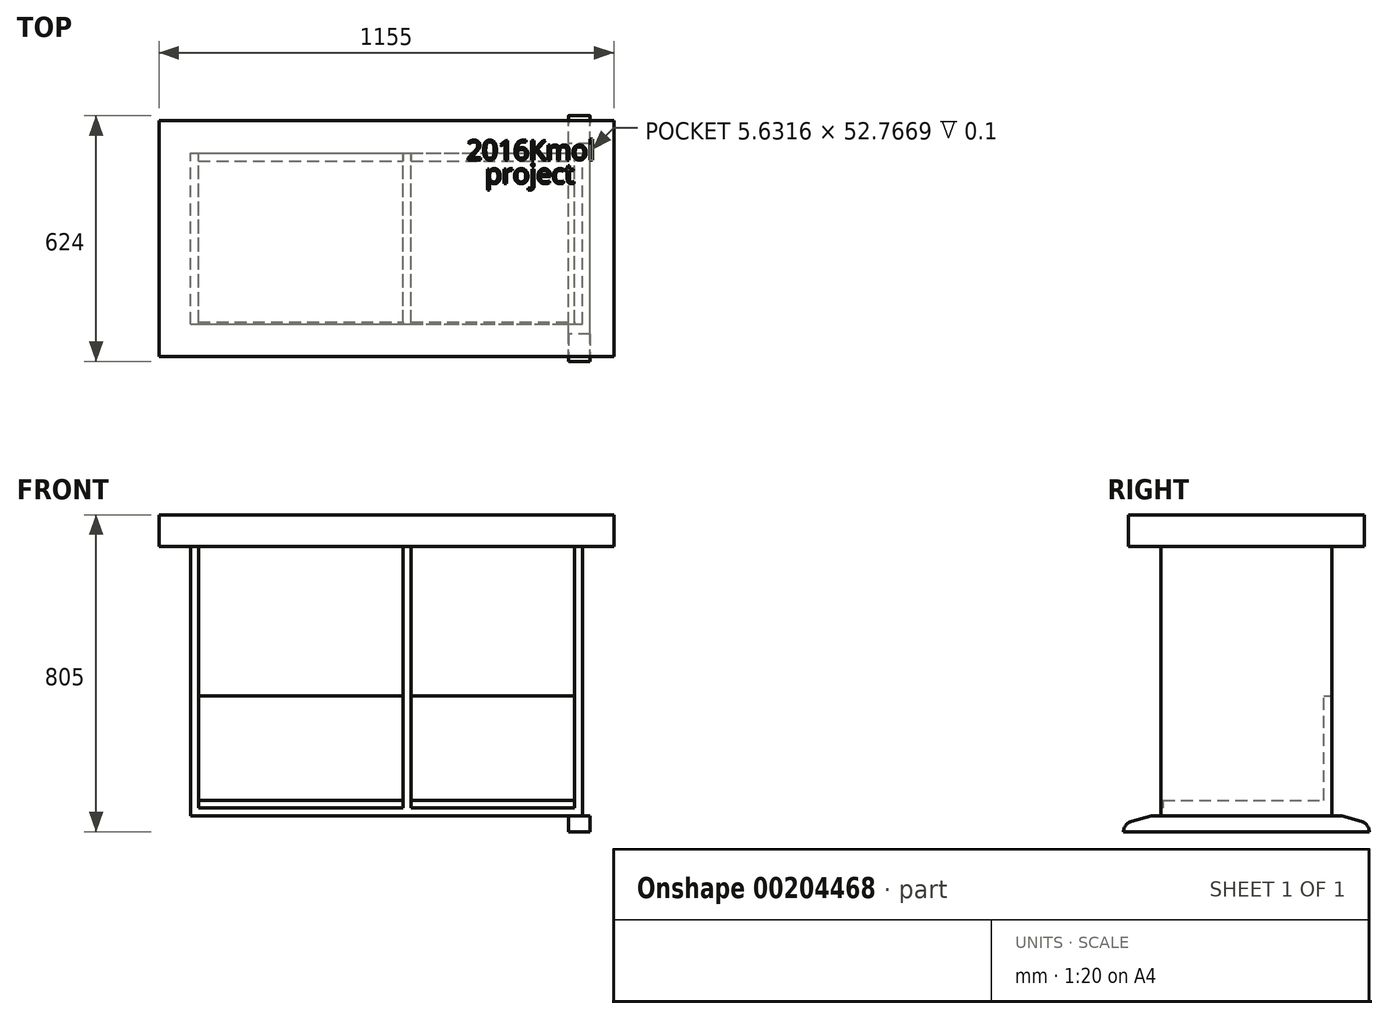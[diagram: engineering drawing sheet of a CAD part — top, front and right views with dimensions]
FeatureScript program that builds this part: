
annotation { "Feature Type Name" : "Feature", "Feature Type Description" : "" }
export const myFeature = defineFeature(function(context is Context, id is Id, definition is map)
    precondition{}
    {
        {
            var Q0;
            Q0=qCreatedBy(makeId("Top.planeOp"),FACE);
            cPlane(context, id + "F0", {"entities" : qUnion([Q0]), "cplaneType" : CPlaneType.OFFSET, "offset" : 770 * mm, "width" : 150 * mm, "height" : 150 * mm});
        }
        {
            var Q0;
            Q0=qCreatedBy(id+"F0.planeOp",FACE);
            var sketch = newSketch(context, id + "F1", { "sketchPlane" : qUnion([Q0])});
            skLineSegment(sketch, "E0.bottom", {"start": v(545, 0) * mm, "end": v(1700, 0) * mm});
            skLineSegment(sketch, "E0.top", {"start": v(545, 600) * mm, "end": v(1700, 600) * mm});
            skLineSegment(sketch, "E0.left", {"start": v(545, 0) * mm, "end": v(545, 600) * mm});
            skLineSegment(sketch, "E0.right", {"start": v(1700, 0) * mm, "end": v(1700, 600) * mm});
            skSolve(sketch);
        }
        {
            var Q0;
            Q0=makeQuery(id+"F1.imprint","IMPRINT",FACE,{"disambiguationData":[TD([[makeQuery(id+"F1.imprint","IMPRINT",EDGE,{"derivedFrom":sQuery(id+"F1.wireOp",EDGE,"E0.bottom")}),1.0]])]});
            extrude(context, id + "F2", {"entities" : qUnion([Q0]), "depth" : 80 * mm});
        }
        {
            var Q0;
            Q0=makeQuery(id+"F2.opExtrude","CAP_FACE",FACE,{"disambiguationData":[OSD([sQuery(id+"F1.wireOp",EDGE,"E0.bottom"),sQuery(id+"F1.wireOp",EDGE,"E0.top"),sQuery(id+"F1.wireOp",EDGE,"E0.left"),sQuery(id+"F1.wireOp",EDGE,"E0.right")])],"isStart":true});
            var sketch = newSketch(context, id + "F3", { "sketchPlane" : qUnion([Q0])});
            skLineSegment(sketch, "E1.bottom", {"start": v(1600, -83) * mm, "end": v(1620, -83) * mm});
            skLineSegment(sketch, "E1.top", {"start": v(1600, -517) * mm, "end": v(1620, -517) * mm});
            skLineSegment(sketch, "E1.left", {"start": v(1600, -83) * mm, "end": v(1600, -517) * mm});
            skLineSegment(sketch, "E1.right", {"start": v(1620, -83) * mm, "end": v(1620, -517) * mm});
            skLineSegment(sketch, "E2.bottom", {"start": v(1165, -83) * mm, "end": v(1185, -83) * mm});
            skLineSegment(sketch, "E2.top", {"start": v(1165, -517) * mm, "end": v(1185, -517) * mm});
            skLineSegment(sketch, "E2.left", {"start": v(1185, -83) * mm, "end": v(1185, -517) * mm});
            skLineSegment(sketch, "E2.right", {"start": v(1165, -83) * mm, "end": v(1165, -517) * mm});
            skLineSegment(sketch, "E3.bottom", {"start": v(625, -83) * mm, "end": v(645, -83) * mm});
            skLineSegment(sketch, "E3.top", {"start": v(625, -517) * mm, "end": v(645, -517) * mm});
            skLineSegment(sketch, "E3.left", {"start": v(625, -83) * mm, "end": v(625, -517) * mm});
            skLineSegment(sketch, "E3.right", {"start": v(645, -83) * mm, "end": v(645, -517) * mm});
            skSolve(sketch);
        }
        {
            var Q0;
            Q0=qSketchRegion(id+"F3",true);
            extrude(context, id + "F4", {"entities" : qUnion([Q0]), "operationType" : NewBodyOperationType.ADD, "depth" : 685 * mm});
        }
        {
            var Q0;
            Q0=makeQuery(id+"F4.opExtrude","CAP_FACE",FACE,{"disambiguationData":[OSD([sQuery(id+"F3.wireOp",EDGE,"E3.bottom"),sQuery(id+"F3.wireOp",EDGE,"E3.top"),sQuery(id+"F3.wireOp",EDGE,"E3.left"),sQuery(id+"F3.wireOp",EDGE,"E3.right")])],"isStart":false});
            var sketch = newSketch(context, id + "F5", { "sketchPlane" : qUnion([Q0])});
            skLineSegment(sketch, "E4.bottom", {"start": v(625, -517) * mm, "end": v(1620, -517) * mm});
            skLineSegment(sketch, "E4.top", {"start": v(625, -83) * mm, "end": v(1620, -83) * mm});
            skLineSegment(sketch, "E4.left", {"start": v(625, -517) * mm, "end": v(625, -83) * mm});
            skLineSegment(sketch, "E4.right", {"start": v(1620, -517) * mm, "end": v(1620, -83) * mm});
            skSolve(sketch);
        }
        {
            var Q0;
            {var subQ2=sQuery(id+"F5.wireOp",EDGE,"E4.right");Q0=makeQuery(id+"F5.imprint","IMPRINT",FACE,{"disambiguationData":[TD([[makeQuery(id+"F5.imprint","IMPRINT",EDGE,{"derivedFrom":subQ2}),1.0]])]});}
            extrude(context, id + "F6", {"entities" : qUnion([Q0]), "operationType" : NewBodyOperationType.ADD, "oppositeDirection" : true, "depth" : 40 * mm});
        }
        {
            var Q0;
            Q0=makeQuery(id+"F6.boolean.opBoolean","MERGE",FACE,{"derivedFrom":[makeQuery(id+"F4.opExtrude","SWEPT_FACE",FACE,{"disambiguationData":[OSD([sQuery(id+"F3.wireOp",EDGE,"E1.bottom")])]}),makeQuery(id+"F4.opExtrude","SWEPT_FACE",FACE,{"disambiguationData":[OSD([sQuery(id+"F3.wireOp",EDGE,"E2.bottom")])]}),makeQuery(id+"F4.opExtrude","SWEPT_FACE",FACE,{"disambiguationData":[OSD([sQuery(id+"F3.wireOp",EDGE,"E3.bottom")])]}),makeQuery(id+"F6.opExtrude","SWEPT_FACE",FACE,{"disambiguationData":[OSD([sQuery(id+"F5.wireOp",EDGE,"E4.top")])]})]});
            var sketch = newSketch(context, id + "F7", { "sketchPlane" : qUnion([Q0])});
            skLineSegment(sketch, "E5.bottom", {"start": v(645, 125) * mm, "end": v(1165, 125) * mm});
            skLineSegment(sketch, "E5.top", {"start": v(645, 105) * mm, "end": v(1165, 105) * mm});
            skLineSegment(sketch, "E5.left", {"start": v(645, 125) * mm, "end": v(645, 105) * mm});
            skLineSegment(sketch, "E5.right", {"start": v(1165, 125) * mm, "end": v(1165, 105) * mm});
            skLineSegment(sketch, "E6.bottom", {"start": v(1185, 125) * mm, "end": v(1600, 125) * mm});
            skLineSegment(sketch, "E6.top", {"start": v(1185, 105) * mm, "end": v(1600, 105) * mm});
            skLineSegment(sketch, "E6.left", {"start": v(1185, 125) * mm, "end": v(1185, 105) * mm});
            skLineSegment(sketch, "E6.right", {"start": v(1600, 125) * mm, "end": v(1600, 105) * mm});
            skSolve(sketch);
        }
        {
            var Q0;
            Q0=qSketchRegion(id+"F7",true);
            extrude(context, id + "F8", {"entities" : qUnion([Q0]), "operationType" : NewBodyOperationType.REMOVE, "oppositeDirection" : true, "depth" : 5 * mm});
        }
        {
            var Q0;
            Q0=makeQuery(id+"F8.boolean.opBoolean","MERGE",FACE,{"derivedFrom":[makeQuery(id+"F4.opExtrude","SWEPT_FACE",FACE,{"disambiguationData":[OSD([sQuery(id+"F3.wireOp",EDGE,"E1.left")])]}),makeQuery(id+"F8.opExtrude","SWEPT_FACE",FACE,{"disambiguationData":[OSD([sQuery(id+"F7.wireOp",EDGE,"E6.right")])]})]});
            var sketch = newSketch(context, id + "F9", { "sketchPlane" : qUnion([Q0])});
            skLineSegment(sketch, "E7.bottom", {"start": v(-517, 390) * mm, "end": v(-497, 390) * mm});
            skLineSegment(sketch, "E7.top", {"start": v(-517, 125) * mm, "end": v(-497, 125) * mm});
            skLineSegment(sketch, "E7.left", {"start": v(-517, 390) * mm, "end": v(-517, 125) * mm});
            skLineSegment(sketch, "E7.right", {"start": v(-497, 390) * mm, "end": v(-497, 125) * mm});
            skSolve(sketch);
        }
        {
            var Q0;
            Q0=qSketchRegion(id+"F9",true);
            var Q1;
            Q1=makeQuery(id+"F8.boolean.opBoolean","MERGE",FACE,{"derivedFrom":[makeQuery(id+"F4.opExtrude","SWEPT_FACE",FACE,{"disambiguationData":[OSD([sQuery(id+"F3.wireOp",EDGE,"E3.right")])]}),makeQuery(id+"F8.opExtrude","SWEPT_FACE",FACE,{"disambiguationData":[OSD([sQuery(id+"F7.wireOp",EDGE,"E5.left")])]})]});
            extrude(context, id + "F10", {"entities" : qUnion([Q0]), "operationType" : NewBodyOperationType.ADD, "endBound" : BoundingType.UP_TO_SURFACE, "endBoundEntityFace" : qUnion([Q1]), "depth" : 25 * mm});
        }
        {
            var Q0;
            Q0=makeQuery(id+"F2.opExtrude","CAP_FACE",FACE,{"disambiguationData":[OSD([sQuery(id+"F1.wireOp",EDGE,"E0.bottom"),sQuery(id+"F1.wireOp",EDGE,"E0.top"),sQuery(id+"F1.wireOp",EDGE,"E0.left"),sQuery(id+"F1.wireOp",EDGE,"E0.right")])],"isStart":false});
            var sketch = newSketch(context, id + "F11", { "sketchPlane" : qUnion([Q0])});
            skText(sketch, "E8", { "text": "2016Kmol", "fontName": "OpenSans-Regular.ttf"});
            skText(sketch, "E9", { "text": "project", "fontName": "OpenSans-Regular.ttf"});
            const initialGuessF11  = {"E8": [1.32592, 0.5, 1, 0, 0.05], "E9": [1.37295, 0.44, 1, 0, 0.05]};
            skSetInitialGuess(sketch, initialGuessF11);
            skSolve(sketch);
        }
        {
            var Q0;
            Q0=qSketchRegion(id+"F11",true);
            extrude(context, id + "F12", {"entities" : qUnion([Q0]), "operationType" : NewBodyOperationType.REMOVE, "oppositeDirection" : true, "depth" : 0.1 * mm});
        }
        {
            var Q0;
            Q0=makeQuery(id+"F4.opExtrude","SWEPT_FACE",FACE,{"disambiguationData":[OSD([sQuery(id+"F3.wireOp",EDGE,"E1.right")])]});
            var sketch = newSketch(context, id + "F13", { "sketchPlane" : qUnion([Q0])});
            skLineSegment(sketch, "E10", {"start": v(58, 85) * mm, "end": v(8, 71.24) * mm});
            skArc(sketch, "E11", {"start": v(8, 71.24) * mm, "mid": v(-6.43, 61.5) * mm, "end": v(-12, 45) * mm});
            skLineSegment(sketch, "E12", {"start": v(-12, 45) * mm, "end": v(300, 45) * mm});
            skPoint(sketch, "E12.endSnap0", {"position": v(300, 85) * mm});
            skLineSegment(sketch, "E13", {"start": v(58, 85) * mm, "end": v(300, 85) * mm});
            skLineSegment(sketch, "E14", {"start": v(300, 85) * mm, "end": v(300, -33.8) * mm, "construction": true});
            skLineSegment(sketch, "E15.MirrorCS", {"start": v(542, 85) * mm, "end": v(300, 85) * mm});
            skLineSegment(sketch, "E16.MirrorCS", {"start": v(612, 45) * mm, "end": v(300, 45) * mm});
            skLineSegment(sketch, "E17.MirrorCS", {"start": v(542, 85) * mm, "end": v(592, 71.24) * mm});
            skArc(sketch, "E18.MirrorCS", {"start": v(592, 71.24) * mm, "mid": v(606.43, 61.5) * mm, "end": v(612, 45) * mm});
            skSolve(sketch);
        }
        {
            var Q0;
            Q0=qSketchRegion(id+"F13",true);
            extrude(context, id + "F14", {"entities" : qUnion([Q0]), "operationType" : NewBodyOperationType.ADD, "depth" : 20 * mm, "hasSecondDirection" : true, "secondDirectionOppositeDirection" : true, "secondDirectionDepth" : 35 * mm});
        }
        {
            var Q0;
            Q0=qCreatedBy(makeId("Right.planeOp"),FACE);
            cPlane(context, id + "F15", {"entities" : qUnion([Q0]), "cplaneType" : CPlaneType.OFFSET, "offset" : 1122.5 * mm, "width" : 150 * mm, "height" : 150 * mm});
        }
    });
